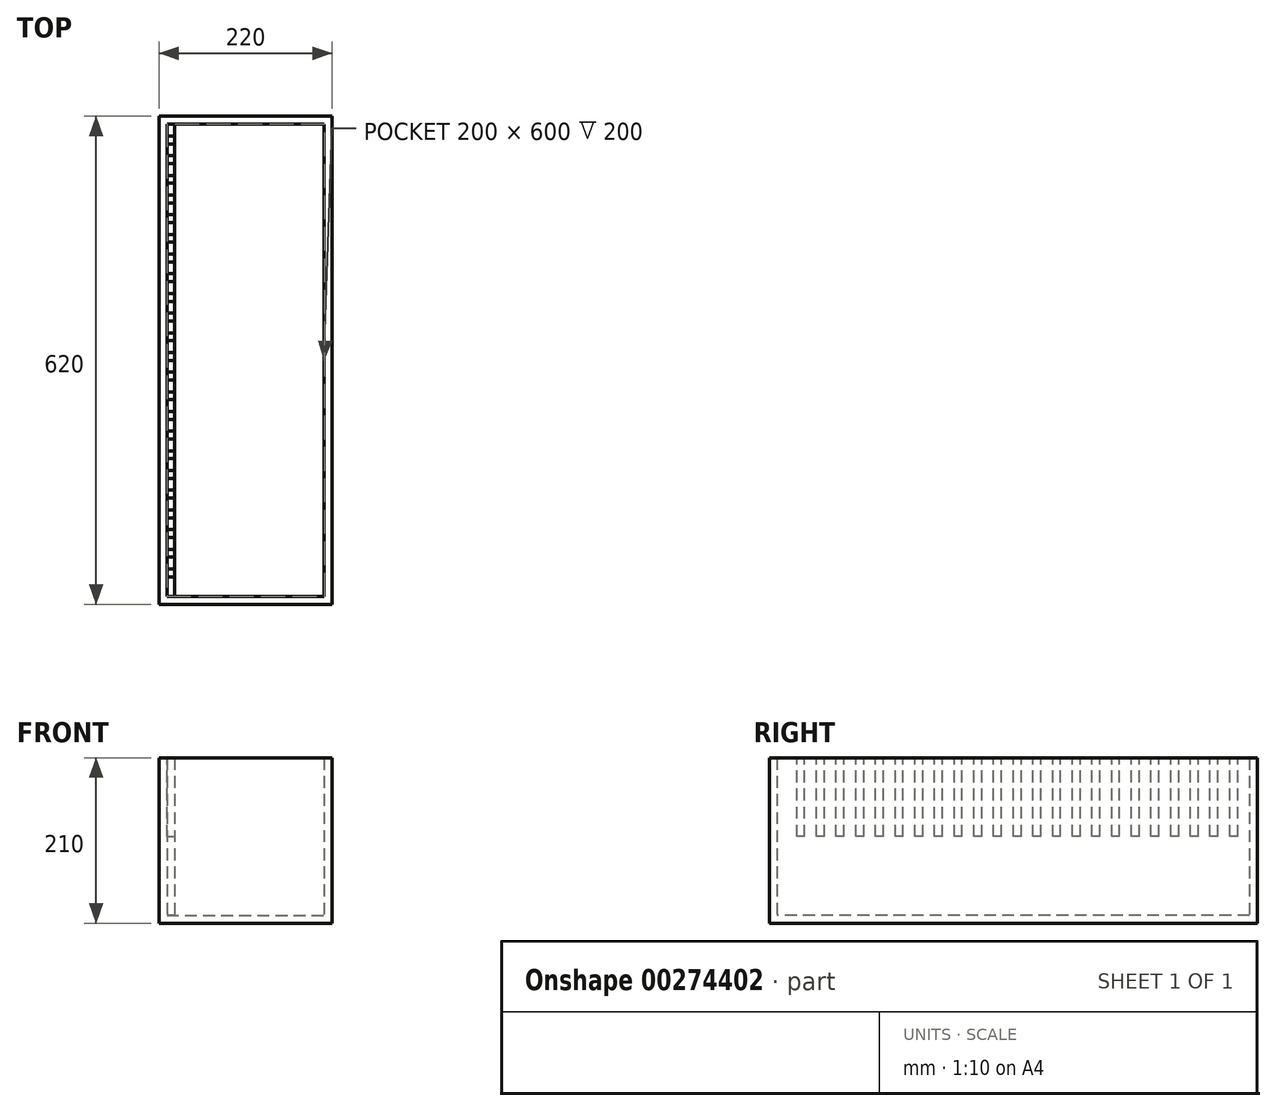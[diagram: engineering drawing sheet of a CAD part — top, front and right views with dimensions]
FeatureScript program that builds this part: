
annotation { "Feature Type Name" : "Feature", "Feature Type Description" : "" }
export const myFeature = defineFeature(function(context is Context, id is Id, definition is map)
    precondition{}
    {
        {
            var Q0;
            Q0=qCreatedBy(makeId("Top.planeOp"),FACE);
            var sketch = newSketch(context, id + "F0", { "sketchPlane" : qUnion([Q0])});
            skLineSegment(sketch, "E0.bottom", {"start": v(-162.27, 548.02) * mm, "end": v(37.73, 548.02) * mm});
            skLineSegment(sketch, "E0.top", {"start": v(-162.27, -51.98) * mm, "end": v(37.73, -51.98) * mm});
            skLineSegment(sketch, "E0.left", {"start": v(-162.27, 548.02) * mm, "end": v(-162.27, -51.98) * mm});
            skLineSegment(sketch, "E0.right", {"start": v(37.73, 548.02) * mm, "end": v(37.73, -51.98) * mm});
            skLineSegment(sketch, "E1.0", {"start": v(-172.27, 558.02) * mm, "end": v(47.73, 558.02) * mm});
            skLineSegment(sketch, "E1.1", {"start": v(-172.27, 558.02) * mm, "end": v(-172.27, -61.98) * mm});
            skLineSegment(sketch, "E1.2", {"start": v(-172.27, -61.98) * mm, "end": v(47.73, -61.98) * mm});
            skLineSegment(sketch, "E1.3", {"start": v(47.73, 558.02) * mm, "end": v(47.73, -61.98) * mm});
            skSolve(sketch);
        }
        {
            var Q0;
            Q0=makeQuery(id+"F0.imprint","IMPRINT",FACE,{"disambiguationData":[TD([[makeQuery(id+"F0.imprint","IMPRINT",EDGE,{"derivedFrom":sQuery(id+"F0.wireOp",EDGE,"E0.bottom")}),1.0]])]});
            extrude(context, id + "F1", {"entities" : qUnion([Q0]), "depth" : 200 * mm, "offsetDistance" : 25 * mm});
        }
        {
            var Q0;
            Q0=makeQuery(id+"F0.imprint","IMPRINT",FACE,{"disambiguationData":[TD([[makeQuery(id+"F0.imprint","IMPRINT",EDGE,{"derivedFrom":sQuery(id+"F0.wireOp",EDGE,"E0.bottom")}),-1.0]])]});
            var Q1;
            Q1=makeQuery(id+"F0.imprint","IMPRINT",FACE,{"disambiguationData":[TD([[makeQuery(id+"F0.imprint","IMPRINT",EDGE,{"derivedFrom":sQuery(id+"F0.wireOp",EDGE,"E0.bottom")}),1.0]])]});
            extrude(context, id + "F2", {"entities" : qUnion([Q0, Q1]), "operationType" : NewBodyOperationType.ADD, "oppositeDirection" : true, "depth" : 10 * mm, "offsetDistance" : 25 * mm});
        }
        {
            var Q0;
            Q0=makeQuery(id+"F1.opExtrude","SWEPT_FACE",FACE,{"disambiguationData":[OSD([sQuery(id+"F0.wireOp",EDGE,"E0.left")])]});
            var sketch = newSketch(context, id + "F3", { "sketchPlane" : qUnion([Q0])});
            skLineSegment(sketch, "E2.0.0", {"start": v(-51.98, 0) * mm, "end": v(548.02, 0) * mm});
            skLineSegment(sketch, "E2.0.1", {"start": v(548.02, 0) * mm, "end": v(548.02, 200) * mm});
            skLineSegment(sketch, "E2.0.2", {"start": v(548.02, 200) * mm, "end": v(-51.98, 200) * mm});
            skLineSegment(sketch, "E2.0.3", {"start": v(-51.98, 200) * mm, "end": v(-51.98, 0) * mm});
            skSolve(sketch);
        }
        {
            var Q0;
            Q0 = qSketchRegion(id + "F3", true);
            extrude(context, id + "F4", {"entities" : qUnion([Q0]), "depth" : 10 * mm, "offsetDistance" : 25 * mm});
        }
        {
            var Q0;
            Q0=makeQuery(id+"F4.opExtrude","CAP_FACE",FACE,{"disambiguationData":[OSD([sQuery(id+"F3.wireOp",EDGE,"E2.0.0"),sQuery(id+"F3.wireOp",EDGE,"E2.0.1"),sQuery(id+"F3.wireOp",EDGE,"E2.0.2"),sQuery(id+"F3.wireOp",EDGE,"E2.0.3")])],"isStart":false});
            var sketch = newSketch(context, id + "F5", { "sketchPlane" : qUnion([Q0])});
            skLineSegment(sketch, "E3.bottom", {"start": v(-26.98, 200) * mm, "end": v(-16.98, 200) * mm});
            skLineSegment(sketch, "E3.top", {"start": v(-26.98, 100) * mm, "end": v(-16.98, 100) * mm});
            skLineSegment(sketch, "E3.left", {"start": v(-26.98, 200) * mm, "end": v(-26.98, 100) * mm});
            skLineSegment(sketch, "E3.right", {"start": v(-16.98, 200) * mm, "end": v(-16.98, 100) * mm});
            skLineSegment(sketch, "E4.1.0.0", {"start": v(-1.98, 200) * mm, "end": v(-1.98, 100) * mm});
            skLineSegment(sketch, "E4.1.0.1", {"start": v(-1.98, 200) * mm, "end": v(8.02, 200) * mm});
            skLineSegment(sketch, "E4.1.0.2", {"start": v(8.02, 200) * mm, "end": v(8.02, 100) * mm});
            skLineSegment(sketch, "E4.1.0.3", {"start": v(-1.98, 100) * mm, "end": v(8.02, 100) * mm});
            skLineSegment(sketch, "E4.2.0.0", {"start": v(23.02, 200) * mm, "end": v(23.02, 100) * mm});
            skLineSegment(sketch, "E4.2.0.1", {"start": v(23.02, 200) * mm, "end": v(33.02, 200) * mm});
            skLineSegment(sketch, "E4.2.0.2", {"start": v(33.02, 200) * mm, "end": v(33.02, 100) * mm});
            skLineSegment(sketch, "E4.2.0.3", {"start": v(23.02, 100) * mm, "end": v(33.02, 100) * mm});
            skLineSegment(sketch, "E4.3.0.0", {"start": v(48.02, 200) * mm, "end": v(48.02, 100) * mm});
            skLineSegment(sketch, "E4.3.0.1", {"start": v(48.02, 200) * mm, "end": v(58.02, 200) * mm});
            skLineSegment(sketch, "E4.3.0.2", {"start": v(58.02, 200) * mm, "end": v(58.02, 100) * mm});
            skLineSegment(sketch, "E4.3.0.3", {"start": v(48.02, 100) * mm, "end": v(58.02, 100) * mm});
            skLineSegment(sketch, "E4.4.0.0", {"start": v(73.02, 200) * mm, "end": v(73.02, 100) * mm});
            skLineSegment(sketch, "E4.4.0.1", {"start": v(73.02, 200) * mm, "end": v(83.02, 200) * mm});
            skLineSegment(sketch, "E4.4.0.2", {"start": v(83.02, 200) * mm, "end": v(83.02, 100) * mm});
            skLineSegment(sketch, "E4.4.0.3", {"start": v(73.02, 100) * mm, "end": v(83.02, 100) * mm});
            skLineSegment(sketch, "E4.5.0.0", {"start": v(98.02, 200) * mm, "end": v(98.02, 100) * mm});
            skLineSegment(sketch, "E4.5.0.1", {"start": v(98.02, 200) * mm, "end": v(108.02, 200) * mm});
            skLineSegment(sketch, "E4.5.0.2", {"start": v(108.02, 200) * mm, "end": v(108.02, 100) * mm});
            skLineSegment(sketch, "E4.5.0.3", {"start": v(98.02, 100) * mm, "end": v(108.02, 100) * mm});
            skLineSegment(sketch, "E4.6.0.0", {"start": v(123.02, 200) * mm, "end": v(123.02, 100) * mm});
            skLineSegment(sketch, "E4.6.0.1", {"start": v(123.02, 200) * mm, "end": v(133.02, 200) * mm});
            skLineSegment(sketch, "E4.6.0.2", {"start": v(133.02, 200) * mm, "end": v(133.02, 100) * mm});
            skLineSegment(sketch, "E4.6.0.3", {"start": v(123.02, 100) * mm, "end": v(133.02, 100) * mm});
            skLineSegment(sketch, "E4.7.0.0", {"start": v(148.02, 200) * mm, "end": v(148.02, 100) * mm});
            skLineSegment(sketch, "E4.7.0.1", {"start": v(148.02, 200) * mm, "end": v(158.02, 200) * mm});
            skLineSegment(sketch, "E4.7.0.2", {"start": v(158.02, 200) * mm, "end": v(158.02, 100) * mm});
            skLineSegment(sketch, "E4.7.0.3", {"start": v(148.02, 100) * mm, "end": v(158.02, 100) * mm});
            skLineSegment(sketch, "E4.8.0.0", {"start": v(173.02, 200) * mm, "end": v(173.02, 100) * mm});
            skLineSegment(sketch, "E4.8.0.1", {"start": v(173.02, 200) * mm, "end": v(183.02, 200) * mm});
            skLineSegment(sketch, "E4.8.0.2", {"start": v(183.02, 200) * mm, "end": v(183.02, 100) * mm});
            skLineSegment(sketch, "E4.8.0.3", {"start": v(173.02, 100) * mm, "end": v(183.02, 100) * mm});
            skLineSegment(sketch, "E4.9.0.0", {"start": v(198.02, 200) * mm, "end": v(198.02, 100) * mm});
            skLineSegment(sketch, "E4.9.0.1", {"start": v(198.02, 200) * mm, "end": v(208.02, 200) * mm});
            skLineSegment(sketch, "E4.9.0.2", {"start": v(208.02, 200) * mm, "end": v(208.02, 100) * mm});
            skLineSegment(sketch, "E4.9.0.3", {"start": v(198.02, 100) * mm, "end": v(208.02, 100) * mm});
            skLineSegment(sketch, "E4.10.0.0", {"start": v(223.02, 200) * mm, "end": v(223.02, 100) * mm});
            skLineSegment(sketch, "E4.10.0.1", {"start": v(223.02, 200) * mm, "end": v(233.02, 200) * mm});
            skLineSegment(sketch, "E4.10.0.2", {"start": v(233.02, 200) * mm, "end": v(233.02, 100) * mm});
            skLineSegment(sketch, "E4.10.0.3", {"start": v(223.02, 100) * mm, "end": v(233.02, 100) * mm});
            skLineSegment(sketch, "E4.11.0.0", {"start": v(248.02, 200) * mm, "end": v(248.02, 100) * mm});
            skLineSegment(sketch, "E4.11.0.1", {"start": v(248.02, 200) * mm, "end": v(258.02, 200) * mm});
            skLineSegment(sketch, "E4.11.0.2", {"start": v(258.02, 200) * mm, "end": v(258.02, 100) * mm});
            skLineSegment(sketch, "E4.11.0.3", {"start": v(248.02, 100) * mm, "end": v(258.02, 100) * mm});
            skLineSegment(sketch, "E4.12.0.0", {"start": v(273.02, 200) * mm, "end": v(273.02, 100) * mm});
            skLineSegment(sketch, "E4.12.0.1", {"start": v(273.02, 200) * mm, "end": v(283.02, 200) * mm});
            skLineSegment(sketch, "E4.12.0.2", {"start": v(283.02, 200) * mm, "end": v(283.02, 100) * mm});
            skLineSegment(sketch, "E4.12.0.3", {"start": v(273.02, 100) * mm, "end": v(283.02, 100) * mm});
            skLineSegment(sketch, "E4.13.0.0", {"start": v(298.02, 200) * mm, "end": v(298.02, 100) * mm});
            skLineSegment(sketch, "E4.13.0.1", {"start": v(298.02, 200) * mm, "end": v(308.02, 200) * mm});
            skLineSegment(sketch, "E4.13.0.2", {"start": v(308.02, 200) * mm, "end": v(308.02, 100) * mm});
            skLineSegment(sketch, "E4.13.0.3", {"start": v(298.02, 100) * mm, "end": v(308.02, 100) * mm});
            skLineSegment(sketch, "E4.14.0.0", {"start": v(323.02, 200) * mm, "end": v(323.02, 100) * mm});
            skLineSegment(sketch, "E4.14.0.1", {"start": v(323.02, 200) * mm, "end": v(333.02, 200) * mm});
            skLineSegment(sketch, "E4.14.0.2", {"start": v(333.02, 200) * mm, "end": v(333.02, 100) * mm});
            skLineSegment(sketch, "E4.14.0.3", {"start": v(323.02, 100) * mm, "end": v(333.02, 100) * mm});
            skLineSegment(sketch, "E4.15.0.0", {"start": v(348.02, 200) * mm, "end": v(348.02, 100) * mm});
            skLineSegment(sketch, "E4.15.0.1", {"start": v(348.02, 200) * mm, "end": v(358.02, 200) * mm});
            skLineSegment(sketch, "E4.15.0.2", {"start": v(358.02, 200) * mm, "end": v(358.02, 100) * mm});
            skLineSegment(sketch, "E4.15.0.3", {"start": v(348.02, 100) * mm, "end": v(358.02, 100) * mm});
            skLineSegment(sketch, "E4.16.0.0", {"start": v(373.02, 200) * mm, "end": v(373.02, 100) * mm});
            skLineSegment(sketch, "E4.16.0.1", {"start": v(373.02, 200) * mm, "end": v(383.02, 200) * mm});
            skLineSegment(sketch, "E4.16.0.2", {"start": v(383.02, 200) * mm, "end": v(383.02, 100) * mm});
            skLineSegment(sketch, "E4.16.0.3", {"start": v(373.02, 100) * mm, "end": v(383.02, 100) * mm});
            skLineSegment(sketch, "E4.17.0.0", {"start": v(398.02, 200) * mm, "end": v(398.02, 100) * mm});
            skLineSegment(sketch, "E4.17.0.1", {"start": v(398.02, 200) * mm, "end": v(408.02, 200) * mm});
            skLineSegment(sketch, "E4.17.0.2", {"start": v(408.02, 200) * mm, "end": v(408.02, 100) * mm});
            skLineSegment(sketch, "E4.17.0.3", {"start": v(398.02, 100) * mm, "end": v(408.02, 100) * mm});
            skLineSegment(sketch, "E4.18.0.0", {"start": v(423.02, 200) * mm, "end": v(423.02, 100) * mm});
            skLineSegment(sketch, "E4.18.0.1", {"start": v(423.02, 200) * mm, "end": v(433.02, 200) * mm});
            skLineSegment(sketch, "E4.18.0.2", {"start": v(433.02, 200) * mm, "end": v(433.02, 100) * mm});
            skLineSegment(sketch, "E4.18.0.3", {"start": v(423.02, 100) * mm, "end": v(433.02, 100) * mm});
            skLineSegment(sketch, "E4.19.0.0", {"start": v(448.02, 200) * mm, "end": v(448.02, 100) * mm});
            skLineSegment(sketch, "E4.19.0.1", {"start": v(448.02, 200) * mm, "end": v(458.02, 200) * mm});
            skLineSegment(sketch, "E4.19.0.2", {"start": v(458.02, 200) * mm, "end": v(458.02, 100) * mm});
            skLineSegment(sketch, "E4.19.0.3", {"start": v(448.02, 100) * mm, "end": v(458.02, 100) * mm});
            skLineSegment(sketch, "E4.20.0.0", {"start": v(473.02, 200) * mm, "end": v(473.02, 100) * mm});
            skLineSegment(sketch, "E4.20.0.1", {"start": v(473.02, 200) * mm, "end": v(483.02, 200) * mm});
            skLineSegment(sketch, "E4.20.0.2", {"start": v(483.02, 200) * mm, "end": v(483.02, 100) * mm});
            skLineSegment(sketch, "E4.20.0.3", {"start": v(473.02, 100) * mm, "end": v(483.02, 100) * mm});
            skLineSegment(sketch, "E4.21.0.0", {"start": v(498.02, 200) * mm, "end": v(498.02, 100) * mm});
            skLineSegment(sketch, "E4.21.0.1", {"start": v(498.02, 200) * mm, "end": v(508.02, 200) * mm});
            skLineSegment(sketch, "E4.21.0.2", {"start": v(508.02, 200) * mm, "end": v(508.02, 100) * mm});
            skLineSegment(sketch, "E4.21.0.3", {"start": v(498.02, 100) * mm, "end": v(508.02, 100) * mm});
            skLineSegment(sketch, "E4.22.0.0", {"start": v(523.02, 200) * mm, "end": v(523.02, 100) * mm});
            skLineSegment(sketch, "E4.22.0.1", {"start": v(523.02, 200) * mm, "end": v(533.02, 200) * mm});
            skLineSegment(sketch, "E4.22.0.2", {"start": v(533.02, 200) * mm, "end": v(533.02, 100) * mm});
            skLineSegment(sketch, "E4.22.0.3", {"start": v(523.02, 100) * mm, "end": v(533.02, 100) * mm});
            skLineSegment(sketch, "E4.direction1", {"start": v(-26.98, 100) * mm, "end": v(-1.98, 100) * mm, "construction": true});
            skSolve(sketch);
        }
        {
            var Q0;
            Q0=makeQuery(id+"F5.imprint","IMPRINT",FACE,{"disambiguationData":[TD([[makeQuery(id+"F5.imprint","IMPRINT",EDGE,{"derivedFrom":sQuery(id+"F5.wireOp",EDGE,"E3.bottom")}),1.0]])]});
            var Q1;
            Q1=makeQuery(id+"F5.imprint","IMPRINT",FACE,{"disambiguationData":[TD([[makeQuery(id+"F5.imprint","IMPRINT",EDGE,{"derivedFrom":sQuery(id+"F5.wireOp",EDGE,"E4.1.0.0")}),1.0]])]});
            var Q2;
            Q2=makeQuery(id+"F5.imprint","IMPRINT",FACE,{"disambiguationData":[TD([[makeQuery(id+"F5.imprint","IMPRINT",EDGE,{"derivedFrom":sQuery(id+"F5.wireOp",EDGE,"E4.2.0.0")}),1.0]])]});
            var Q3;
            Q3=makeQuery(id+"F5.imprint","IMPRINT",FACE,{"disambiguationData":[TD([[makeQuery(id+"F5.imprint","IMPRINT",EDGE,{"derivedFrom":sQuery(id+"F5.wireOp",EDGE,"E4.3.0.0")}),1.0]])]});
            var Q4;
            Q4=makeQuery(id+"F5.imprint","IMPRINT",FACE,{"disambiguationData":[TD([[makeQuery(id+"F5.imprint","IMPRINT",EDGE,{"derivedFrom":sQuery(id+"F5.wireOp",EDGE,"E4.4.0.0")}),1.0]])]});
            var Q5;
            Q5=makeQuery(id+"F5.imprint","IMPRINT",FACE,{"disambiguationData":[TD([[makeQuery(id+"F5.imprint","IMPRINT",EDGE,{"derivedFrom":sQuery(id+"F5.wireOp",EDGE,"E4.5.0.0")}),1.0]])]});
            var Q6;
            Q6=makeQuery(id+"F5.imprint","IMPRINT",FACE,{"disambiguationData":[TD([[makeQuery(id+"F5.imprint","IMPRINT",EDGE,{"derivedFrom":sQuery(id+"F5.wireOp",EDGE,"E4.6.0.0")}),1.0]])]});
            var Q7;
            Q7=makeQuery(id+"F5.imprint","IMPRINT",FACE,{"disambiguationData":[TD([[makeQuery(id+"F5.imprint","IMPRINT",EDGE,{"derivedFrom":sQuery(id+"F5.wireOp",EDGE,"E4.7.0.0")}),1.0]])]});
            var Q8;
            Q8=makeQuery(id+"F5.imprint","IMPRINT",FACE,{"disambiguationData":[TD([[makeQuery(id+"F5.imprint","IMPRINT",EDGE,{"derivedFrom":sQuery(id+"F5.wireOp",EDGE,"E4.8.0.0")}),1.0]])]});
            var Q9;
            Q9=makeQuery(id+"F5.imprint","IMPRINT",FACE,{"disambiguationData":[TD([[makeQuery(id+"F5.imprint","IMPRINT",EDGE,{"derivedFrom":sQuery(id+"F5.wireOp",EDGE,"E4.9.0.0")}),1.0]])]});
            var Q10;
            Q10=makeQuery(id+"F5.imprint","IMPRINT",FACE,{"disambiguationData":[TD([[makeQuery(id+"F5.imprint","IMPRINT",EDGE,{"derivedFrom":sQuery(id+"F5.wireOp",EDGE,"E4.10.0.0")}),1.0]])]});
            var Q11;
            Q11=makeQuery(id+"F5.imprint","IMPRINT",FACE,{"disambiguationData":[TD([[makeQuery(id+"F5.imprint","IMPRINT",EDGE,{"derivedFrom":sQuery(id+"F5.wireOp",EDGE,"E4.11.0.0")}),1.0]])]});
            var Q12;
            Q12=makeQuery(id+"F5.imprint","IMPRINT",FACE,{"disambiguationData":[TD([[makeQuery(id+"F5.imprint","IMPRINT",EDGE,{"derivedFrom":sQuery(id+"F5.wireOp",EDGE,"E4.12.0.0")}),1.0]])]});
            var Q13;
            Q13=makeQuery(id+"F5.imprint","IMPRINT",FACE,{"disambiguationData":[TD([[makeQuery(id+"F5.imprint","IMPRINT",EDGE,{"derivedFrom":sQuery(id+"F5.wireOp",EDGE,"E4.13.0.0")}),1.0]])]});
            var Q14;
            Q14=makeQuery(id+"F5.imprint","IMPRINT",FACE,{"disambiguationData":[TD([[makeQuery(id+"F5.imprint","IMPRINT",EDGE,{"derivedFrom":sQuery(id+"F5.wireOp",EDGE,"E4.14.0.0")}),1.0]])]});
            var Q15;
            Q15=makeQuery(id+"F5.imprint","IMPRINT",FACE,{"disambiguationData":[TD([[makeQuery(id+"F5.imprint","IMPRINT",EDGE,{"derivedFrom":sQuery(id+"F5.wireOp",EDGE,"E4.15.0.0")}),1.0]])]});
            var Q16;
            Q16=makeQuery(id+"F5.imprint","IMPRINT",FACE,{"disambiguationData":[TD([[makeQuery(id+"F5.imprint","IMPRINT",EDGE,{"derivedFrom":sQuery(id+"F5.wireOp",EDGE,"E4.16.0.0")}),1.0]])]});
            var Q17;
            Q17=makeQuery(id+"F5.imprint","IMPRINT",FACE,{"disambiguationData":[TD([[makeQuery(id+"F5.imprint","IMPRINT",EDGE,{"derivedFrom":sQuery(id+"F5.wireOp",EDGE,"E4.17.0.0")}),1.0]])]});
            var Q18;
            Q18=makeQuery(id+"F5.imprint","IMPRINT",FACE,{"disambiguationData":[TD([[makeQuery(id+"F5.imprint","IMPRINT",EDGE,{"derivedFrom":sQuery(id+"F5.wireOp",EDGE,"E4.18.0.0")}),1.0]])]});
            var Q19;
            Q19=makeQuery(id+"F5.imprint","IMPRINT",FACE,{"disambiguationData":[TD([[makeQuery(id+"F5.imprint","IMPRINT",EDGE,{"derivedFrom":sQuery(id+"F5.wireOp",EDGE,"E4.19.0.0")}),1.0]])]});
            var Q20;
            Q20=makeQuery(id+"F5.imprint","IMPRINT",FACE,{"disambiguationData":[TD([[makeQuery(id+"F5.imprint","IMPRINT",EDGE,{"derivedFrom":sQuery(id+"F5.wireOp",EDGE,"E4.20.0.0")}),1.0]])]});
            var Q21;
            Q21=makeQuery(id+"F5.imprint","IMPRINT",FACE,{"disambiguationData":[TD([[makeQuery(id+"F5.imprint","IMPRINT",EDGE,{"derivedFrom":sQuery(id+"F5.wireOp",EDGE,"E4.21.0.0")}),1.0]])]});
            var Q22;
            Q22=makeQuery(id+"F5.imprint","IMPRINT",FACE,{"disambiguationData":[TD([[makeQuery(id+"F5.imprint","IMPRINT",EDGE,{"derivedFrom":sQuery(id+"F5.wireOp",EDGE,"E4.22.0.0")}),1.0]])]});
            extrude(context, id + "F6", {"entities" : qUnion([Q0, Q1, Q2, Q3, Q4, Q5, Q6, Q7, Q8, Q9, Q10, Q11, Q12, Q13, Q14, Q15, Q16, Q17, Q18, Q19, Q20, Q21, Q22]), "operationType" : NewBodyOperationType.REMOVE, "endBound" : BoundingType.UP_TO_NEXT, "oppositeDirection" : true, "depth" : 25 * mm, "offsetDistance" : 25 * mm});
        }
    });
